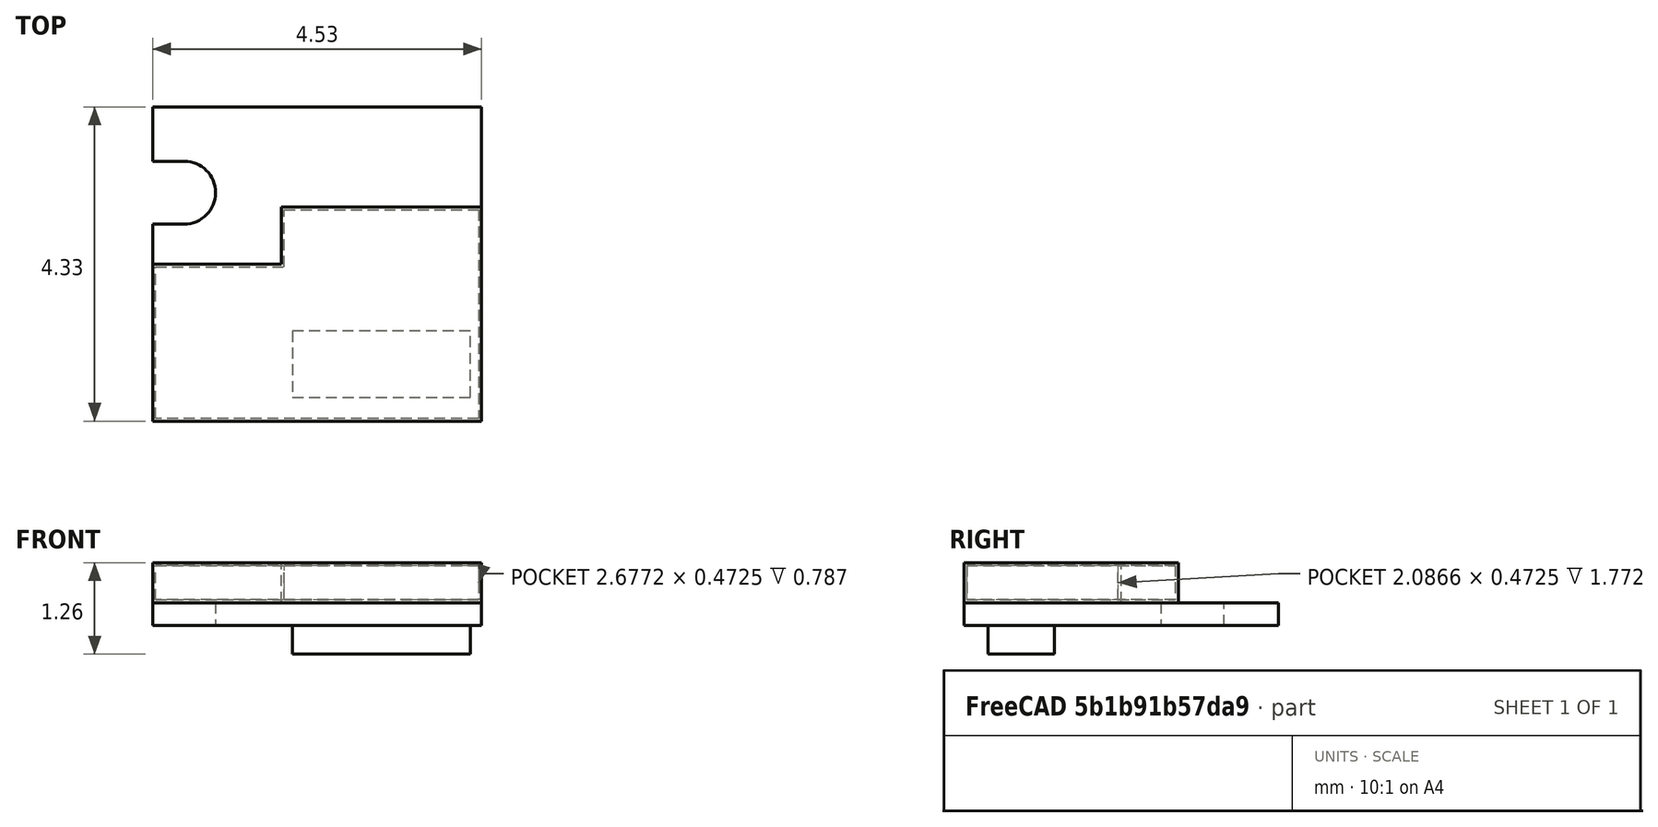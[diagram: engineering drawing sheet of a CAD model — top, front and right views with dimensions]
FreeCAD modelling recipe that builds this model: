
FCSTD DOCUMENT  (FreeCAD 0.16R6706 (Git))
Label: IMBLE
License: All rights reserved
LicenseURL: http://en.wikipedia.org/wiki/All_rights_reserved
objects: Part::Feature×3, Part::FeaturePython×3
note: 6 computed .brp shape members not serialized (recipe doc carries the construction recipe); baked Part::Feature solids carry a one-line shape summary decoded from their .brp

FEATURE [Part::Feature] Part__Feature  label="\X2\30B330F330DD30FC30CD30F330C8\X0\3"
  Placement = pos=(0,0,0) rot=(1,0,0;1.5708rad)
  shape: bbox 11.5 x 7.5 x 1.4 mm, 16 faces (baked)
FEATURE [Part::Feature] Part__Feature001  label="\X2\30B330F330DD30FC30CD30F330C8\X0\1"
  Placement = pos=(0,0,0) rot=(1,0,0;1.5708rad)
  shape: bbox 11.5 x 11 x 0.8 mm, 10 faces (baked)
FEATURE [Part::Feature] Part__Feature002  label="\X2\30B330F330DD30FC30CD30F330C8\X0\2"
  Placement = pos=(0,0,0) rot=(1,0,0;1.5708rad)
  shape: bbox 6.22 x 2.32 x 1 mm, 6 faces (baked)
FEATURE [Part::FeaturePython] Scale  # Draft clone (typed FeaturePython)
  Objects = -> [Part__Feature]
  Placement = pos=(0,0,0) rot=(1,0,0;1.5708rad)
  Scale = (0.3937,0.3937,0.3937)
FEATURE [Part::FeaturePython] Scale001  # Draft clone (typed FeaturePython)
  Objects = -> [Part__Feature001]
  Placement = pos=(0,0,0) rot=(1,0,0;1.5708rad)
  Scale = (0.3937,0.3937,0.3937)
FEATURE [Part::FeaturePython] Scale002  # Draft clone (typed FeaturePython)
  Objects = -> [Part__Feature002]
  Placement = pos=(0,0,0) rot=(1,0,0;1.5708rad)
  Scale = (0.3937,0.3937,0.3937)
